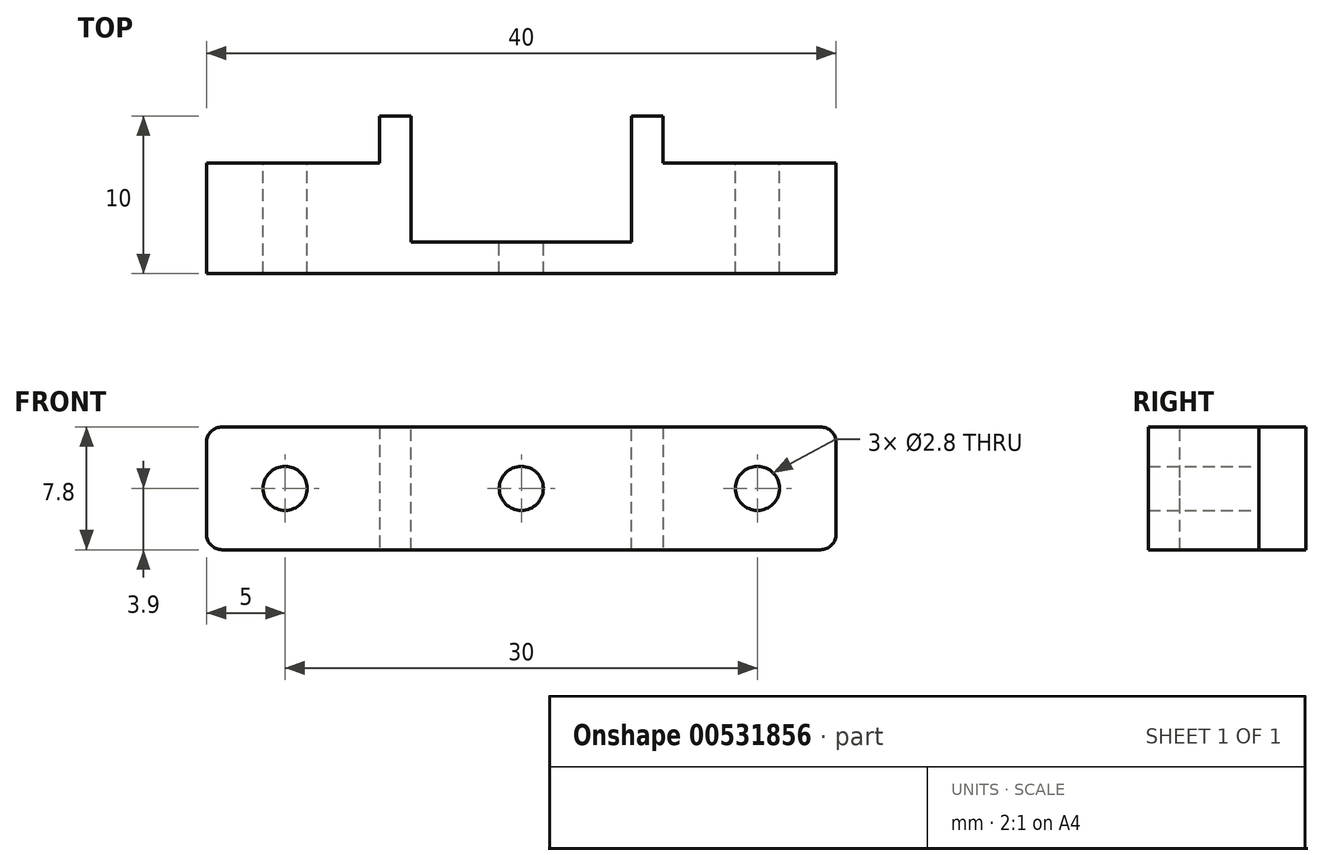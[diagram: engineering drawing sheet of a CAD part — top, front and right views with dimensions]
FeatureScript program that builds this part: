
annotation { "Feature Type Name" : "Feature", "Feature Type Description" : "" }
export const myFeature = defineFeature(function(context is Context, id is Id, definition is map)
    precondition{}
    {
        {
            var Q0;
            Q0=qCreatedBy(makeId("Front.planeOp"),FACE);
            var sketch = newSketch(context, id + "F0", { "sketchPlane" : qUnion([Q0])});
            skLineSegment(sketch, "E0.bottom", {"start": v(0, 0) * mm, "end": v(40, 0) * mm});
            skLineSegment(sketch, "E0.top", {"start": v(0, 7.8) * mm, "end": v(40, 7.8) * mm});
            skLineSegment(sketch, "E0.left", {"start": v(0, 0) * mm, "end": v(0, 7.8) * mm});
            skLineSegment(sketch, "E0.right", {"start": v(40, 0) * mm, "end": v(40, 7.8) * mm});
            skLineSegment(sketch, "E1", {"start": v(0, 3.9) * mm, "end": v(10, 3.9) * mm});
            skCircle(sketch, "E2", {"center": v(5, 3.9) * mm, "radius": 1.4 * mm});
            skLineSegment(sketch, "E3", {"start": v(40, 3.9) * mm, "end": v(30, 3.9) * mm});
            skPoint(sketch, "E3.endSnap0", {"position": v(40, 3.9) * mm});
            skCircle(sketch, "E4", {"center": v(35, 3.9) * mm, "radius": 1.4 * mm});
            skLineSegment(sketch, "E5", {"start": v(20, 7.8) * mm, "end": v(20, 3.9) * mm});
            skCircle(sketch, "E6", {"center": v(20, 3.9) * mm, "radius": 1.4 * mm});
            skSolve(sketch);
        }
        {
            var Q0;
            Q0=qSketchRegion(id+"F0",true);
            extrude(context, id + "F1", {"entities" : qUnion([Q0]), "depth" : 2 * mm});
        }
        {
            var Q0;
            Q0=makeQuery(id+"F1.opExtrude","SWEPT_EDGE",EDGE,{"disambiguationData":[OSD([sQuery(id+"F0.wireOp",EDGE,"E0.top"),sQuery(id+"F0.wireOp",EDGE,"E0.left")])]});
            var Q1;
            Q1=makeQuery(id+"F1.opExtrude","SWEPT_EDGE",EDGE,{"disambiguationData":[OSD([sQuery(id+"F0.wireOp",EDGE,"E0.bottom"),sQuery(id+"F0.wireOp",EDGE,"E0.left")])]});
            var Q2;
            Q2=makeQuery(id+"F1.opExtrude","SWEPT_EDGE",EDGE,{"disambiguationData":[OSD([sQuery(id+"F0.wireOp",EDGE,"E0.top"),sQuery(id+"F0.wireOp",EDGE,"E0.right")])]});
            var Q3;
            Q3=makeQuery(id+"F1.opExtrude","SWEPT_EDGE",EDGE,{"disambiguationData":[OSD([sQuery(id+"F0.wireOp",EDGE,"E0.bottom"),sQuery(id+"F0.wireOp",EDGE,"E0.right")])]});
            fillet(context, id + "F2", {"entities" : qUnion([Q0, Q1, Q2, Q3]), "radius" : 1 * mm, "tangentPropagation" : true, "allowEdgeOverflow" : false});
        }
        {
            var Q0;
            Q0=makeQuery(id+"F1.opExtrude","CAP_FACE",FACE,{"disambiguationData":[OSD([sQuery(id+"F0.wireOp",EDGE,"E0.bottom"),sQuery(id+"F0.wireOp",EDGE,"E0.top"),sQuery(id+"F0.wireOp",EDGE,"E0.left"),sQuery(id+"F0.wireOp",EDGE,"E0.right"),sQuery(id+"F0.wireOp",EDGE,"E2"),sQuery(id+"F0.wireOp",EDGE,"E4"),sQuery(id+"F0.wireOp",EDGE,"E6")])],"isStart":true});
            var sketch = newSketch(context, id + "F3", { "sketchPlane" : qUnion([Q0])});
            skLineSegment(sketch, "E7", {"start": v(-20, 3.9) * mm, "end": v(-13, 3.9) * mm});
            skLineSegment(sketch, "E8", {"start": v(-13, 3.9) * mm, "end": v(-13, 7.8) * mm});
            skLineSegment(sketch, "E9", {"start": v(-13, 7.8) * mm, "end": v(-11, 7.8) * mm});
            skLineSegment(sketch, "E10", {"start": v(-11, 7.8) * mm, "end": v(-11, 0) * mm});
            skLineSegment(sketch, "E11", {"start": v(-11, 0) * mm, "end": v(-13, 0) * mm});
            skLineSegment(sketch, "E12", {"start": v(-13, 0) * mm, "end": v(-13, 3.9) * mm});
            skLineSegment(sketch, "E13", {"start": v(-20, 3.9) * mm, "end": v(-20, 1.78) * mm});
            skLineSegment(sketch, "E14.MirrorCS", {"start": v(-27, 3.9) * mm, "end": v(-27, 7.8) * mm});
            skLineSegment(sketch, "E15.MirrorCS", {"start": v(-27, 7.8) * mm, "end": v(-29, 7.8) * mm});
            skLineSegment(sketch, "E16.MirrorCS", {"start": v(-29, 7.8) * mm, "end": v(-29, 0) * mm});
            skLineSegment(sketch, "E17.MirrorCS", {"start": v(-29, 0) * mm, "end": v(-27, 0) * mm});
            skLineSegment(sketch, "E18.MirrorCS", {"start": v(-27, 0) * mm, "end": v(-27, 3.9) * mm});
            skSolve(sketch);
        }
        {
            var Q0;
            Q0=qSketchRegion(id+"F3",true);
            extrude(context, id + "F4", {"entities" : qUnion([Q0]), "operationType" : NewBodyOperationType.ADD, "depth" : 8 * mm});
        }
        {
            var Q0;
            {var subQ0=sQuery(id+"F0.wireOp",EDGE,"E0.bottom");var subQ1=sQuery(id+"F0.wireOp",EDGE,"E0.top");var subQ2=sQuery(id+"F0.wireOp",EDGE,"E0.left");var subQ3=sQuery(id+"F0.wireOp",EDGE,"E2");Q0=makeQuery(id+"F4.boolean.opBoolean","SPLIT",FACE,{"disambiguationData":[TD([makeQuery(id+"F1.opExtrude","SWEPT_FACE",FACE,{"disambiguationData":[OSD([subQ2])]})])],"derivedFrom":makeQuery(id+"F1.opExtrude","CAP_FACE",FACE,{"disambiguationData":[OSD([subQ0,subQ1,subQ2,sQuery(id+"F0.wireOp",EDGE,"E0.right"),subQ3,sQuery(id+"F0.wireOp",EDGE,"E4"),sQuery(id+"F0.wireOp",EDGE,"E6")])],"isStart":true})});}
            var Q1;
            {var subQ0=sQuery(id+"F0.wireOp",EDGE,"E0.bottom");var subQ1=sQuery(id+"F0.wireOp",EDGE,"E0.right");var subQ2=sQuery(id+"F0.wireOp",EDGE,"E0.top");var subQ3=sQuery(id+"F0.wireOp",EDGE,"E4");Q1=makeQuery(id+"F4.boolean.opBoolean","SPLIT",FACE,{"disambiguationData":[TD([makeQuery(id+"F1.opExtrude","SWEPT_FACE",FACE,{"disambiguationData":[OSD([subQ1])]})])],"derivedFrom":makeQuery(id+"F1.opExtrude","CAP_FACE",FACE,{"disambiguationData":[OSD([subQ0,subQ2,sQuery(id+"F0.wireOp",EDGE,"E0.left"),subQ1,sQuery(id+"F0.wireOp",EDGE,"E2"),subQ3,sQuery(id+"F0.wireOp",EDGE,"E6")])],"isStart":true})});}
            extrude(context, id + "F5", {"entities" : qUnion([Q0, Q1]), "operationType" : NewBodyOperationType.ADD, "depth" : 5 * mm});
        }
    });
